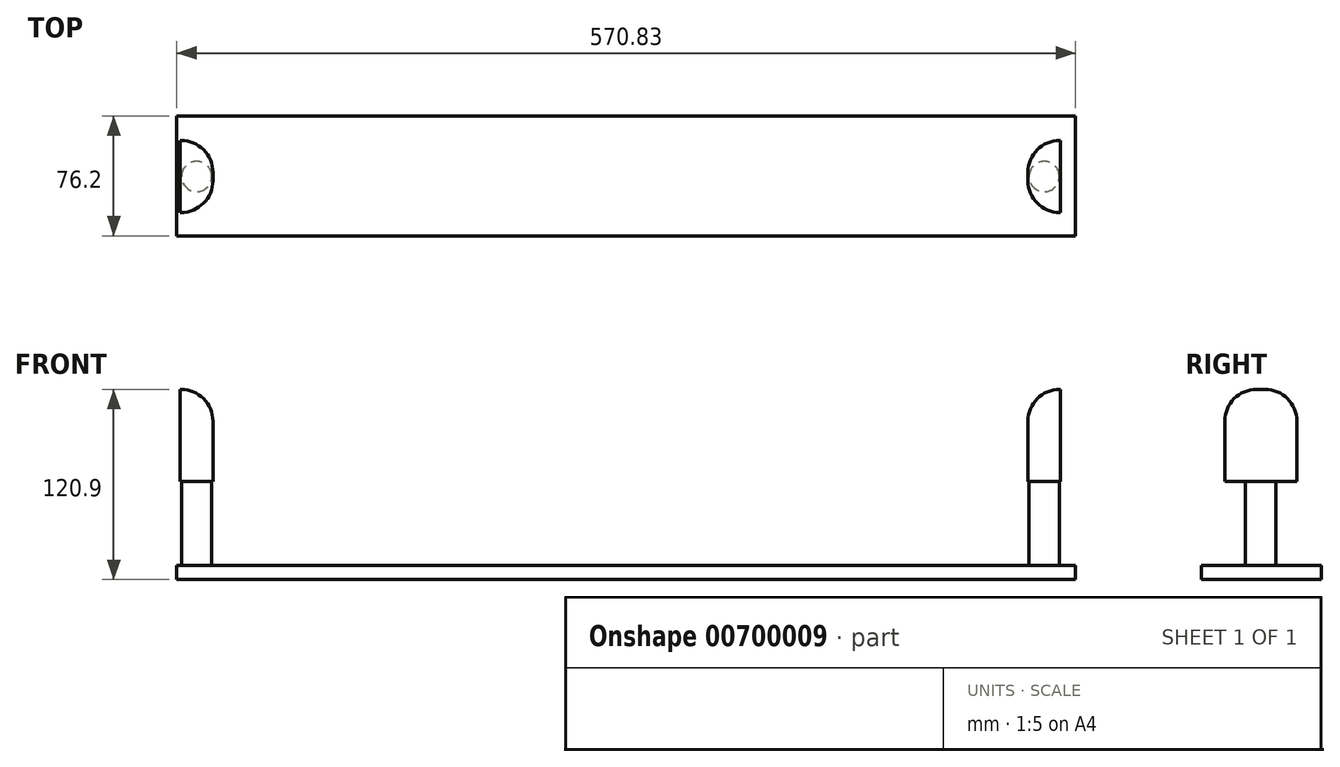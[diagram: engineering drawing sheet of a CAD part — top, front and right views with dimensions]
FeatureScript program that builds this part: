
annotation { "Feature Type Name" : "Feature", "Feature Type Description" : "" }
export const myFeature = defineFeature(function(context is Context, id is Id, definition is map)
    precondition{}
    {
        {
            var Q0;
            Q0=qCreatedBy(makeId("Top.planeOp"),FACE);
            var sketch = newSketch(context, id + "F0", { "sketchPlane" : qUnion([Q0])});
            skLineSegment(sketch, "E0.bottom", {"start": v(-281.8, 45.67) * mm, "end": v(289.03, 45.67) * mm});
            skLineSegment(sketch, "E0.top", {"start": v(-281.8, -30.53) * mm, "end": v(289.03, -30.53) * mm});
            skLineSegment(sketch, "E0.left", {"start": v(-281.8, 45.67) * mm, "end": v(-281.8, -30.53) * mm});
            skLineSegment(sketch, "E0.right", {"start": v(289.03, 45.67) * mm, "end": v(289.03, -30.53) * mm});
            skSolve(sketch);
        }
        {
            var Q0;
            Q0=makeQuery(id+"F0.imprint","IMPRINT",FACE,{"disambiguationData":[TD([[makeQuery(id+"F0.imprint","IMPRINT",EDGE,{"derivedFrom":sQuery(id+"F0.wireOp",EDGE,"E0.bottom")}),-1.0]])]});
            extrude(context, id + "F1", {"entities" : qUnion([Q0]), "depth" : 9.14 * mm, "offsetDistance" : 25.4 * mm});
        }
        {
            var Q0;
            Q0=makeQuery(id+"F1.opExtrude","CAP_FACE",FACE,{"disambiguationData":[OSD([sQuery(id+"F0.wireOp",EDGE,"E0.bottom"),sQuery(id+"F0.wireOp",EDGE,"E0.top"),sQuery(id+"F0.wireOp",EDGE,"E0.left"),sQuery(id+"F0.wireOp",EDGE,"E0.right")])],"isStart":false});
            var sketch = newSketch(context, id + "F2", { "sketchPlane" : qUnion([Q0])});
            skCircle(sketch, "E1", {"center": v(-269.18, 7.17) * mm, "radius": 9.65 * mm});
            skLineSegment(sketch, "E2", {"start": v(0, 57.48) * mm, "end": v(0, -70.96) * mm});
            skCircle(sketch, "E3.MirrorC", {"center": v(269.18, 7.17) * mm, "radius": 9.65 * mm});
            skSolve(sketch);
        }
        {
            var Q0;
            Q0 = qSketchRegion(id + "F2", true);
            extrude(context, id + "F3", {"entities" : qUnion([Q0]), "operationType" : NewBodyOperationType.ADD, "depth" : 53.34 * mm, "offsetDistance" : 25.4 * mm});
        }
        {
            var Q0;
            Q0=makeQuery(id+"F3.opExtrude","CAP_FACE",FACE,{"disambiguationData":[OSD([sQuery(id+"F2.wireOp",EDGE,"E1")])],"isStart":false});
            var sketch = newSketch(context, id + "F4", { "sketchPlane" : qUnion([Q0])});
            skLineSegment(sketch, "E4.bottom", {"start": v(-279.56, 30.09) * mm, "end": v(-258.8, 30.09) * mm});
            skLineSegment(sketch, "E4.top", {"start": v(-279.56, -15.74) * mm, "end": v(-258.8, -15.74) * mm});
            skLineSegment(sketch, "E4.left", {"start": v(-279.56, 30.09) * mm, "end": v(-279.56, -15.74) * mm});
            skLineSegment(sketch, "E4.right", {"start": v(-258.8, 30.09) * mm, "end": v(-258.8, -15.74) * mm});
            skPoint(sketch, "E4.middle", {"position": v(-269.18, 7.17) * mm});
            skLineSegment(sketch, "E5", {"start": v(0, 55.16) * mm, "end": v(0, -46.2) * mm, "construction": true});
            skLineSegment(sketch, "E6.MirrorCS", {"start": v(279.56, 30.09) * mm, "end": v(258.8, 30.09) * mm});
            skLineSegment(sketch, "E7.MirrorCS", {"start": v(279.56, 30.09) * mm, "end": v(279.56, -15.74) * mm});
            skLineSegment(sketch, "E8.MirrorCS", {"start": v(279.56, -15.74) * mm, "end": v(258.8, -15.74) * mm});
            skLineSegment(sketch, "E9.MirrorCS", {"start": v(258.8, 30.09) * mm, "end": v(258.8, -15.74) * mm});
            skSolve(sketch);
        }
        {
            var Q0;
            Q0 = qSketchRegion(id + "F4", true);
            extrude(context, id + "F5", {"entities" : qUnion([Q0]), "operationType" : NewBodyOperationType.ADD, "depth" : 58.42 * mm, "offsetDistance" : 25.4 * mm});
        }
        {
            var Q0;
            Q0=makeQuery(id+"F5.opExtrude","CAP_EDGE",EDGE,{"disambiguationData":[OSD([sQuery(id+"F4.wireOp",EDGE,"E4.top")])],"isStart":false});
            var Q1;
            Q1=makeQuery(id+"F5.opExtrude","CAP_EDGE",EDGE,{"disambiguationData":[OSD([sQuery(id+"F4.wireOp",EDGE,"E4.right")])],"isStart":false});
            var Q2;
            Q2=makeQuery(id+"F5.opExtrude","CAP_EDGE",EDGE,{"disambiguationData":[OSD([sQuery(id+"F4.wireOp",EDGE,"E4.bottom")])],"isStart":false});
            var Q3;
            Q3=makeQuery(id+"F5.opExtrude","SWEPT_EDGE",EDGE,{"disambiguationData":[OSD([sQuery(id+"F4.wireOp",EDGE,"E4.top"),sQuery(id+"F4.wireOp",EDGE,"E4.right")])]});
            var Q4;
            Q4=makeQuery(id+"F5.opExtrude","SWEPT_EDGE",EDGE,{"disambiguationData":[OSD([sQuery(id+"F4.wireOp",EDGE,"E4.bottom"),sQuery(id+"F4.wireOp",EDGE,"E4.right")])]});
            fillet(context, id + "F6", {"entities" : qUnion([Q0, Q1, Q2, Q3, Q4]), "radius" : 20.32 * mm, "tangentPropagation" : true, "allowEdgeOverflow" : false});
        }
        {
            var Q0;
            Q0=makeQuery(id+"F5.opExtrude","CAP_EDGE",EDGE,{"disambiguationData":[OSD([sQuery(id+"F4.wireOp",EDGE,"E9.MirrorCS")])],"isStart":false});
            var Q1;
            Q1=makeQuery(id+"F5.opExtrude","SWEPT_EDGE",EDGE,{"disambiguationData":[OSD([sQuery(id+"F4.wireOp",EDGE,"E6.MirrorCS"),sQuery(id+"F4.wireOp",EDGE,"E9.MirrorCS")])]});
            var Q2;
            Q2=makeQuery(id+"F5.opExtrude","SWEPT_EDGE",EDGE,{"disambiguationData":[OSD([sQuery(id+"F4.wireOp",EDGE,"E8.MirrorCS"),sQuery(id+"F4.wireOp",EDGE,"E9.MirrorCS")])]});
            var Q3;
            Q3=makeQuery(id+"F5.opExtrude","CAP_EDGE",EDGE,{"disambiguationData":[OSD([sQuery(id+"F4.wireOp",EDGE,"E8.MirrorCS")])],"isStart":false});
            var Q4;
            Q4=makeQuery(id+"F5.opExtrude","CAP_EDGE",EDGE,{"disambiguationData":[OSD([sQuery(id+"F4.wireOp",EDGE,"E6.MirrorCS")])],"isStart":false});
            fillet(context, id + "F7", {"entities" : qUnion([Q0, Q1, Q2, Q3, Q4]), "radius" : 20.32 * mm, "tangentPropagation" : true, "allowEdgeOverflow" : false});
        }
    });
